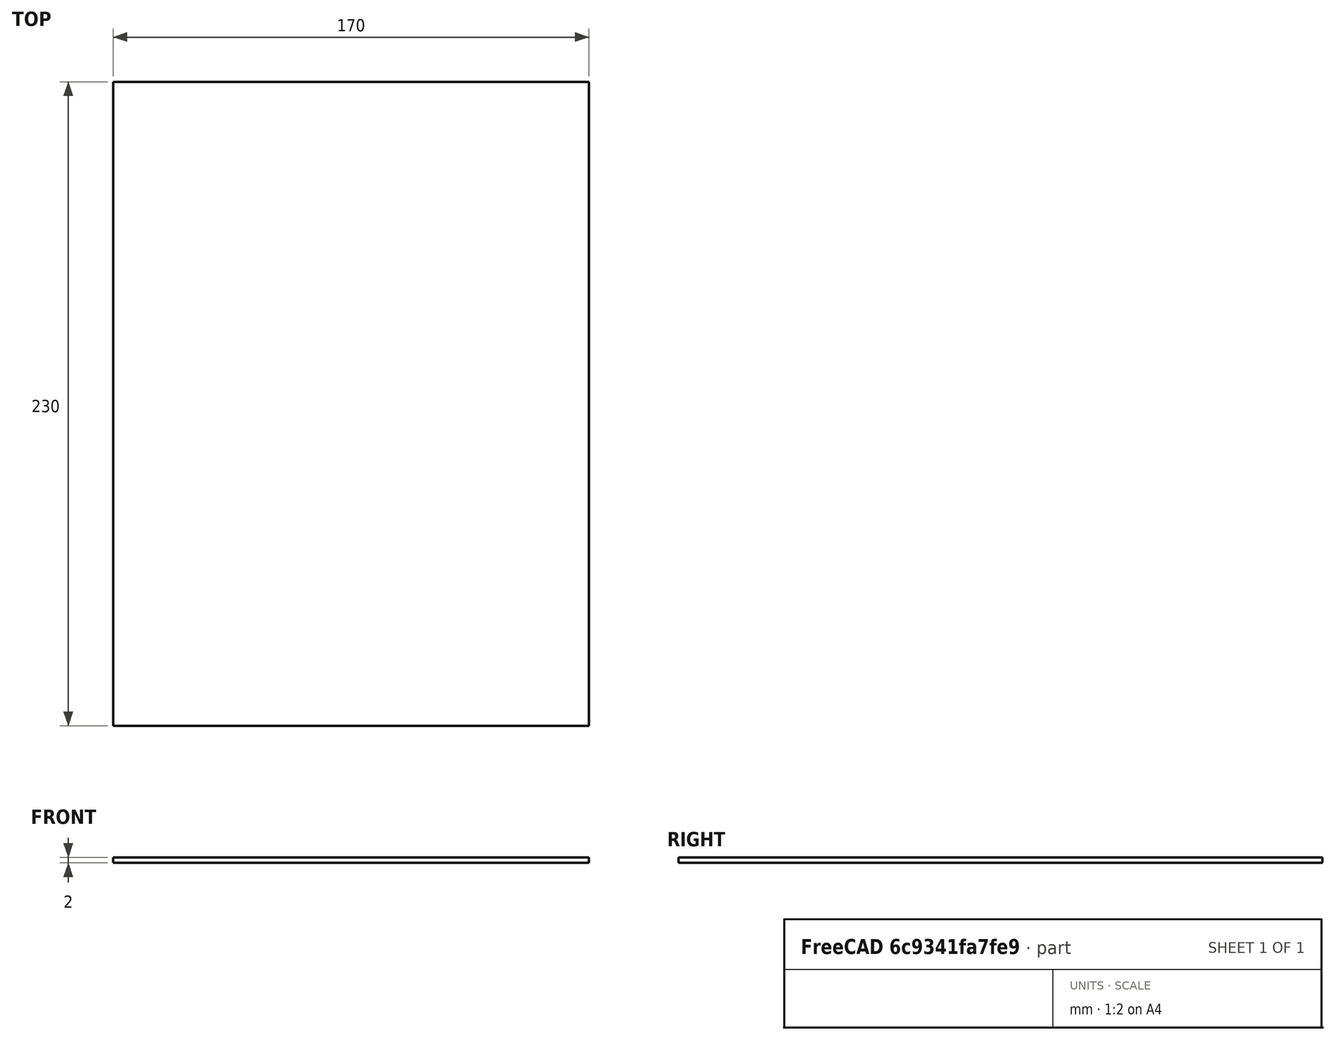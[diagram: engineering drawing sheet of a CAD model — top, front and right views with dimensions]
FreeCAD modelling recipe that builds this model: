
FCSTD DOCUMENT  (FreeCAD 0.17RUnknown)
Label: cam_top
License: All rights reserved
LicenseURL: http://en.wikipedia.org/wiki/All_rights_reserved
objects: Path::FeaturePython×7, Part::FeaturePython×3, App::FeaturePython×1, Path::FeatureCompoundPython×1
note: 5 computed .brp shape members not serialized (recipe doc carries the construction recipe); baked Part::Feature solids carry a one-line shape summary decoded from their .brp

FEATURE [Path::FeaturePython] Default_Tool  label="Default Tool"  # Path/CAM operation (typed FeaturePython)
  HorizFeed = 10
  HorizRapid = 0
  SpindleDir = 0
  SpindleSpeed = 24000
  ToolNumber = 1
  VertFeed = 1.66667
  VertRapid = 0
  expr: Tool.Diameter = 3.1749999999999998
  expr: VertFeed = 100mm / min
  expr: HorizFeed = 600mm / min
  expr: HorizRapid = SetupSheet.HorizRapid
  expr: VertRapid = SetupSheet.VertRapid
FEATURE [Path::FeaturePython] T2__drill  label="T2: drill"  # Path/CAM operation (typed FeaturePython)
  HorizFeed = 10
  HorizRapid = 0
  SpindleDir = 0
  SpindleSpeed = 12000
  ToolNumber = 2
  VertFeed = 1.66667
  VertRapid = 0
  expr: VertFeed = 100mm / min
  expr: HorizFeed = 600mm / min
  expr: HorizRapid = SetupSheet.HorizRapid
  expr: VertRapid = SetupSheet.VertRapid
FEATURE [Part::FeaturePython] Stock001  # WARN: FeaturePython — macro-defined, semantics opaque (R4)
  Height = 2
  Length = 170
  Placement = pos=(0,0,-2) rot=(0,0,1;0rad)
  StockType = CreateBox
  Width = 230
FEATURE [App::FeaturePython] SetupSheet  # Path/CAM operation (typed FeaturePython)
  ClearanceHeightExpression = StartDepth+SetupSheet.ClearanceHeightOffset
  ClearanceHeightOffset = 2
  FinalDepthExpression = OpFinalDepth
  HorizRapid = 0
  SafeHeightExpression = StartDepth+SetupSheet.SafeHeightOffset
  SafeHeightOffset = 3
  StartDepthExpression = OpStartDepth
  StepDownExpression = OpToolDiameter
  VertRapid = 0
FEATURE [Part::FeaturePython] center_01  # a2plus imported part (geometry in sourceFile) (typed FeaturePython)
  Placement = pos=(39,62,-2) rot=(0,0,1;0rad)
  fixedPosition = false
  sourceFile = <userpath>/hs/fly/cad/center.FCStd
  timeLastImport = 1.5368e+09
  updateColors = true
FEATURE [Part::FeaturePython] Clone  label="Base-arm_01"  # Draft clone (typed FeaturePython)
  AttacherType = Attacher::AttachEngine3D
  Fuse = false
  Objects = -> [center_01]
  PathResource = Base
  Placement = pos=(39,62,-2) rot=(0,0,1;0rad)
  Scale = (1,1,1)
FEATURE [Path::FeaturePython] Drilling  # Path/CAM operation (typed FeaturePython)
  Active = true
  AddTipLength = false
  Base = -> [Clone]
  ClearanceHeight = 2
  DwellEnabled = false
  DwellTime = 0
  FinalDepth = -4
  OpFinalDepth = -2
  OpStartDepth = 0
  OpToolDiameter = 3
  PeckDepth = 0
  PeckEnabled = false
  RetractHeight = 10
  ReturnLevel = 0
  SafeHeight = 3
  StartDepth = 0
  ToolController = -> T2__drill
  expr: ClearanceHeight = StartDepth + SetupSheet.ClearanceHeightOffset
  expr: SafeHeight = StartDepth + SetupSheet.SafeHeightOffset
  expr: FinalDepth = -4
  expr: StartDepth = OpStartDepth
FEATURE [Path::FeaturePython] Contour  # Path/CAM operation (typed FeaturePython)
  Active = true
  AreaParams:
    OpenMode = 0
    Angle = 45.0
    MinArcPoints = 4
    Coplanar = 2
    Tolerance = 1e-07
    CleanDistance = 0.0
    PocketExtraOffset = 0.0
    RoundPrecision = 0.0
    AngleShift = 0.0
    SubjectFill = 0
    PocketMode = 0
    Simplify = False
    SectionTolerance = 1e-06
    MaxArcPoints = 100
    Offset = 1.5875
    Accuracy = 0.01
    PocketStepover = 0.0
    ClipFill = 0
    ToolRadius = 1.0
    Outline = False
    ClipperScale = 10000000.0
    FromCenter = False
    Explode = False
    EndType = 0
    Shift = 0.0
    ExtraPass = 0
    Project = False
    JoinType = 0
    Thicken = False
    Stepdown = 1.0
    SectionMode = 2
    MiterLimit = 2.0
    Deflection = 0.01
    Reorient = True
    FitArcs = True
    SectionCount = -1
    SectionOffset = 0.0
    Stepover = 0.0
    Unit = 1.0
    Fill = 0
  ClearanceHeight = 2
  Direction = 0
  FinalDepth = -3
  JoinType = 0
  MiterLimit = 0.1
  OffsetExtra = 0
  OpFinalDepth = -2
  OpStartDepth = 0
  OpToolDiameter = 3.175
  PathParams = {'resume_height': 3.0, 'feedrate': 10.0, 'verbose': True, 'orientation': 1, 'return_end': True, 'preamble': False, 'retraction': 2.0, 'feedrate_v': 1.666666666667}
  SafeHeight = 3
  Side = 0
  StartDepth = 0
  StartPoint = (0,0,0)
  StepDown = 1
  ToolController = -> Default_Tool
  UseComp = true
  UseStartPoint = false
  expr: ClearanceHeight = StartDepth + SetupSheet.ClearanceHeightOffset
  expr: SafeHeight = StartDepth + SetupSheet.SafeHeightOffset
  expr: StepDown = 1
  expr: FinalDepth = -3
  expr: StartDepth = OpStartDepth
FEATURE [Path::FeaturePython] Pocket_Shape001  # Path/CAM operation (typed FeaturePython)
  Active = true
  AreaParams:
    OpenMode = 0
    Angle = 45.0
    MinArcPoints = 4
    Coplanar = 0
    Tolerance = 1e-07
    CleanDistance = 0.0
    PocketExtraOffset = 0.0
    RoundPrecision = 0.0
    AngleShift = 0.0
    SubjectFill = 0
    PocketMode = 2
    Simplify = False
    SectionTolerance = 1e-06
    MaxArcPoints = 100
    Offset = 0.0
    Accuracy = 0.01
    PocketStepover = 3.175
    ClipFill = 0
    ToolRadius = 1.5875
    Outline = False
    ClipperScale = 10000000.0
    FromCenter = True
    Explode = False
    EndType = 0
    Shift = 0.0
    ExtraPass = 0
    Project = False
    JoinType = 0
    Thicken = False
    Stepdown = 1.0
    SectionMode = 2
    MiterLimit = 2.0
    Deflection = 0.01
    Reorient = True
    FitArcs = True
    SectionCount = -1
    SectionOffset = 0.0
    Stepover = 0.0
    Unit = 1.0
    Fill = 0
  Base = -> [Clone]
  ClearanceHeight = 2
  CutMode = 0
  ExtraOffset = 0
  FinalDepth = -2
  FinishDepth = 0
  KeepToolDown = false
  MinTravel = false
  OffsetPattern = 1
  OpFinalDepth = -2
  OpStartDepth = 0
  OpToolDiameter = 3.175
  PathParams = {'resume_height': 3.0, 'feedrate': 10.0, 'verbose': True, 'orientation': 1, 'return_end': True, 'preamble': False, 'retraction': 2.0, 'feedrate_v': 1.666666666667}
  SafeHeight = 3
  StartAt = 0
  StartDepth = 0
  StartPoint = (0,0,0)
  StepDown = 0.5
  StepOver = 100
  ToolController = -> Default_Tool
  UseStartPoint = false
  ZigZagAngle = 45
  expr: ClearanceHeight = StartDepth + SetupSheet.ClearanceHeightOffset
  expr: SafeHeight = StartDepth + SetupSheet.SafeHeightOffset
  expr: StepDown = 0.5
  expr: FinalDepth = OpFinalDepth
  expr: StartDepth = OpStartDepth
FEATURE [Path::FeaturePython] TagDressup  # Path/CAM operation (typed FeaturePython)
  Angle = 75
  Base = -> Contour
  Height = 2.5
  Positions = (5) [(65.1565,62.0199,0),(17.414,14.9544,0),(12.8435,61.9801,0),(39.29,98.89,0),(60.59,14.25,0)]
  Radius = 1
  SegmentationFactor = 50
  Width = 2.79
FEATURE [Path::FeatureCompoundPython] Operations  # Path/CAM operation (typed FeaturePython)
  Group = -> [Drilling,Pocket_Shape001,TagDressup]
  UsePlacements = false
FEATURE [Path::FeaturePython] Job  # Path/CAM operation (typed FeaturePython)
  Base = -> Clone
  GeometryTolerance = 0.01
  Operations = -> Operations
  PostProcessor = 5
  PostProcessorOutputFile = <userpath>/hs/fly/cad/gcode/arm
  SetupSheet = -> SetupSheet
  Stock = -> Stock001
  ToolController = -> [Default_Tool,T2__drill]
